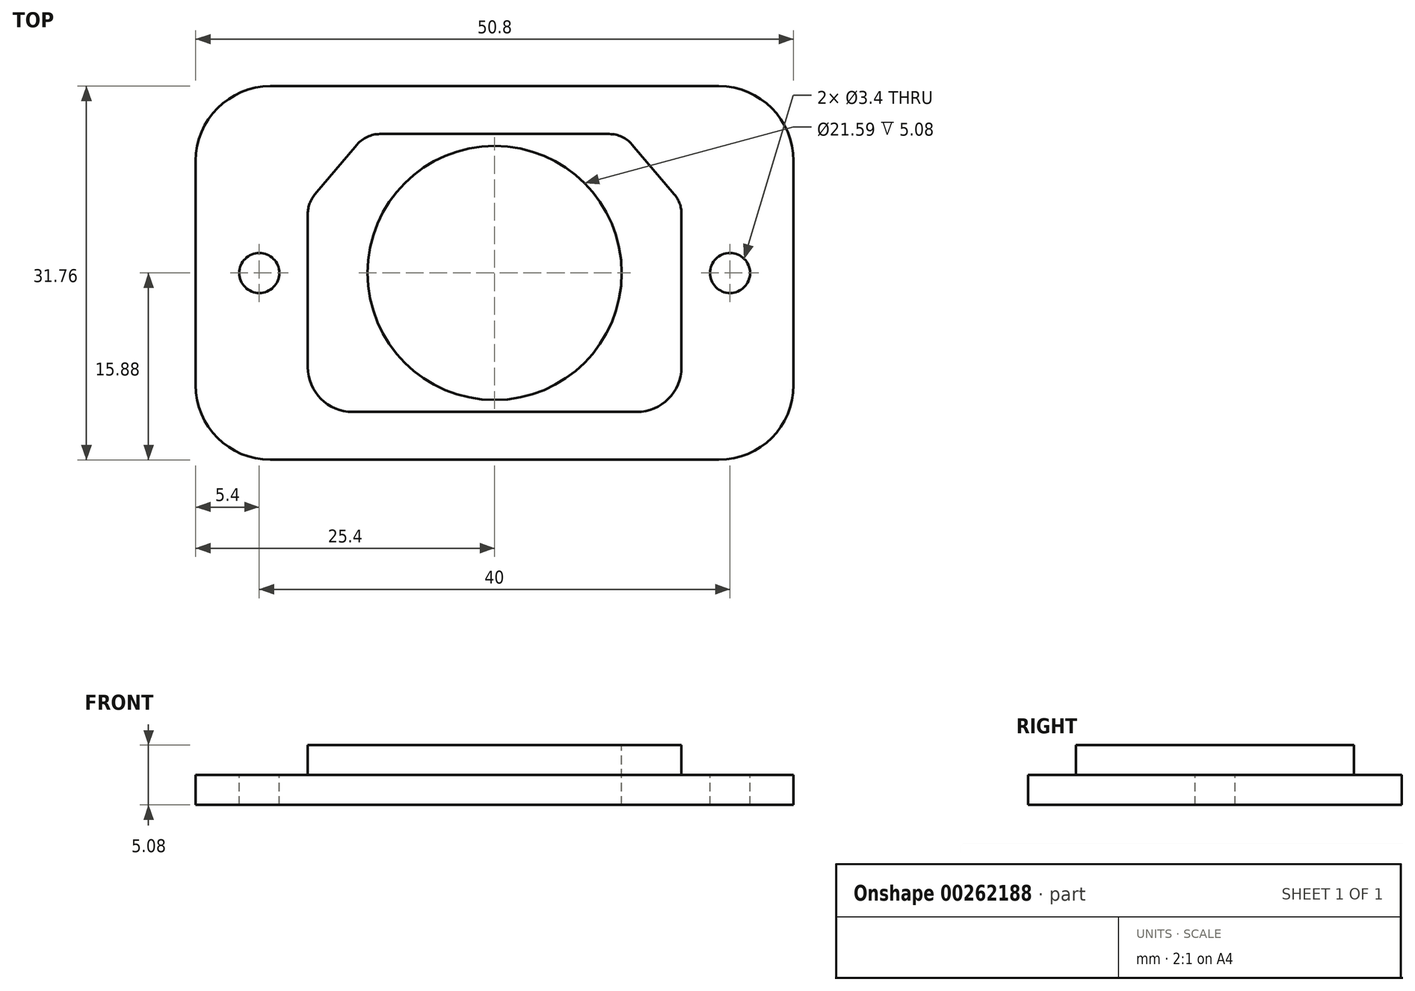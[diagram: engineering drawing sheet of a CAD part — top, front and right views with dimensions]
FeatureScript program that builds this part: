
annotation { "Feature Type Name" : "Feature", "Feature Type Description" : "" }
export const myFeature = defineFeature(function(context is Context, id is Id, definition is map)
    precondition{}
    {
        {
            var Q0;
            Q0=qCreatedBy(makeId("Top.planeOp"),FACE);
            var sketch = newSketch(context, id + "F0", { "sketchPlane" : qUnion([Q0])});
            skLineSegment(sketch, "E0.bottom", {"start": v(19.05, -15.87) * mm, "end": v(-19.05, -15.88) * mm});
            skLineSegment(sketch, "E0.top", {"start": v(19.05, 15.88) * mm, "end": v(-19.05, 15.87) * mm});
            skLineSegment(sketch, "E0.left", {"start": v(25.4, -9.52) * mm, "end": v(25.4, 9.53) * mm});
            skLineSegment(sketch, "E0.right", {"start": v(-25.4, -9.53) * mm, "end": v(-25.4, 9.52) * mm});
            skPoint(sketch, "E0.middle", {"position": v(0, 0) * mm});
            skPoint(sketch, "E1.visualSharp", {"position": v(-25.4, 15.87) * mm});
            skArc(sketch, "E1.filletArc", {"start": v(-19.05, 15.88) * mm, "mid": v(-23.54, 14.02) * mm, "end": v(-25.4, 9.53) * mm});
            skPoint(sketch, "E2.visualSharp", {"position": v(-25.4, -15.88) * mm});
            skArc(sketch, "E2.filletArc", {"start": v(-25.4, -9.53) * mm, "mid": v(-23.54, -14.02) * mm, "end": v(-19.05, -15.88) * mm});
            skPoint(sketch, "E3.visualSharp", {"position": v(25.4, 15.88) * mm});
            skArc(sketch, "E3.filletArc", {"start": v(25.4, 9.53) * mm, "mid": v(23.54, 14.02) * mm, "end": v(19.05, 15.88) * mm});
            skPoint(sketch, "E4.visualSharp", {"position": v(25.4, -15.87) * mm});
            skArc(sketch, "E4.filletArc", {"start": v(19.05, -15.87) * mm, "mid": v(23.54, -14.02) * mm, "end": v(25.4, -9.52) * mm});
            skSolve(sketch);
        }
        {
            var Q0;
            Q0 = qSketchRegion(id + "F0", true);
            extrude(context, id + "F1", {"entities" : qUnion([Q0]), "depth" : 2.54 * mm});
        }
        {
            var Q0;
            Q0=makeQuery(id+"F1.opExtrude","CAP_FACE",FACE,{"disambiguationData":[OSD([sQuery(id+"F0.wireOp",EDGE,"E0.bottom"),sQuery(id+"F0.wireOp",EDGE,"E0.top"),sQuery(id+"F0.wireOp",EDGE,"E0.left"),sQuery(id+"F0.wireOp",EDGE,"E0.right"),sQuery(id+"F0.wireOp",EDGE,"E1.filletArc"),sQuery(id+"F0.wireOp",EDGE,"E2.filletArc"),sQuery(id+"F0.wireOp",EDGE,"E3.filletArc"),sQuery(id+"F0.wireOp",EDGE,"E4.filletArc")])],"isStart":false});
            var sketch = newSketch(context, id + "F2", { "sketchPlane" : qUnion([Q0])});
            skLineSegment(sketch, "E5.bottom", {"start": v(12.06, -11.81) * mm, "end": v(-12.06, -11.81) * mm});
            skLineSegment(sketch, "E5.top", {"start": v(9.75, 11.81) * mm, "end": v(-9.75, 11.81) * mm});
            skLineSegment(sketch, "E5.left", {"start": v(15.88, -8) * mm, "end": v(15.88, 5.04) * mm});
            skLineSegment(sketch, "E5.right", {"start": v(-15.88, -8) * mm, "end": v(-15.88, 5.04) * mm});
            skPoint(sketch, "E5.middle", {"position": v(0, 0) * mm});
            skLineSegment(sketch, "E6", {"start": v(-15.27, 6.68) * mm, "end": v(-11.68, 10.91) * mm});
            skLineSegment(sketch, "E7.MirrorCS", {"start": v(15.27, 6.68) * mm, "end": v(11.68, 10.91) * mm});
            skPoint(sketch, "E8.orphan", {"position": v(-15.88, 11.81) * mm});
            skPoint(sketch, "E9.orphan", {"position": v(15.88, 11.81) * mm});
            skPoint(sketch, "E10.visualSharp", {"position": v(-15.88, -11.81) * mm});
            skArc(sketch, "E10.filletArc", {"start": v(-15.88, -8) * mm, "mid": v(-14.76, -10.7) * mm, "end": v(-12.06, -11.81) * mm});
            skPoint(sketch, "E11.visualSharp", {"position": v(15.88, -11.81) * mm});
            skArc(sketch, "E11.filletArc", {"start": v(12.06, -11.81) * mm, "mid": v(14.76, -10.7) * mm, "end": v(15.88, -8) * mm});
            skPoint(sketch, "E12.visualSharp", {"position": v(15.88, 5.97) * mm});
            skArc(sketch, "E12.filletArc", {"start": v(15.88, 5.04) * mm, "mid": v(15.72, 5.91) * mm, "end": v(15.27, 6.68) * mm});
            skPoint(sketch, "E13.visualSharp", {"position": v(-15.88, 5.97) * mm});
            skArc(sketch, "E13.filletArc", {"start": v(-15.27, 6.68) * mm, "mid": v(-15.72, 5.91) * mm, "end": v(-15.88, 5.04) * mm});
            skPoint(sketch, "E14.visualSharp", {"position": v(-10.92, 11.81) * mm});
            skArc(sketch, "E14.filletArc", {"start": v(-9.75, 11.81) * mm, "mid": v(-10.81, 11.58) * mm, "end": v(-11.68, 10.91) * mm});
            skPoint(sketch, "E15.visualSharp", {"position": v(10.92, 11.81) * mm});
            skArc(sketch, "E15.filletArc", {"start": v(11.68, 10.91) * mm, "mid": v(10.81, 11.58) * mm, "end": v(9.75, 11.81) * mm});
            skSolve(sketch);
        }
        {
            var Q0;
            Q0 = qSketchRegion(id + "F2", true);
            extrude(context, id + "F3", {"entities" : qUnion([Q0]), "operationType" : NewBodyOperationType.ADD, "depth" : 2.54 * mm});
        }
        {
            var Q0;
            Q0=makeQuery(id+"F3.opExtrude","CAP_FACE",FACE,{"disambiguationData":[OSD([sQuery(id+"F2.wireOp",EDGE,"E5.bottom"),sQuery(id+"F2.wireOp",EDGE,"E5.top"),sQuery(id+"F2.wireOp",EDGE,"E5.left"),sQuery(id+"F2.wireOp",EDGE,"E5.right"),sQuery(id+"F2.wireOp",EDGE,"E6"),sQuery(id+"F2.wireOp",EDGE,"E7.MirrorCS"),sQuery(id+"F2.wireOp",EDGE,"E10.filletArc"),sQuery(id+"F2.wireOp",EDGE,"E11.filletArc"),sQuery(id+"F2.wireOp",EDGE,"E12.filletArc"),sQuery(id+"F2.wireOp",EDGE,"E13.filletArc"),sQuery(id+"F2.wireOp",EDGE,"E14.filletArc"),sQuery(id+"F2.wireOp",EDGE,"E15.filletArc")])],"isStart":false});
            var sketch = newSketch(context, id + "F4", { "sketchPlane" : qUnion([Q0])});
            skCircle(sketch, "E16", {"center": v(0, 0) * mm, "radius": 10.8 * mm});
            skCircle(sketch, "E17", {"center": v(-20, 0) * mm, "radius": 1.7 * mm});
            skCircle(sketch, "E18.MirrorC", {"center": v(20, 0) * mm, "radius": 1.7 * mm});
            skSolve(sketch);
        }
        {
            var Q0;
            Q0 = qSketchRegion(id + "F4", true);
            extrude(context, id + "F5", {"entities" : qUnion([Q0]), "operationType" : NewBodyOperationType.REMOVE, "endBound" : BoundingType.THROUGH_ALL, "oppositeDirection" : true, "depth" : 25.4 * mm});
        }
    });
